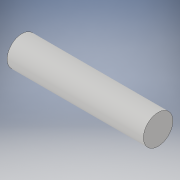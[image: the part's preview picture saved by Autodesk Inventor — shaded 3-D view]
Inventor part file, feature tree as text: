
AUTODESK INVENTOR PART (.ipt)
format: ipt  version: 2017 (Build 210142000, 142)  size: 88,064 bytes
history: native  units: in
note: dims shown in document units (in); Inventor stores cm internally (conversion verified against a paired STEP export)
features: extrude x1, sketch x1
ambient origin geometry x8: Origin, YZ Plane, XZ Plane, XY Plane, X Axis, Y Axis, Z Axis, Center Point
bodies: Solid1 (feature_tree)
feature tree (2):
  extrude  "Extrusion1"  Depth=10.41in TaperAngle=0.0deg
  sketch  "Sketch1"  dims[d0=2.25in d1=10.41in d2=0.0in]
